# Revit family: QF_ELECTROLUXPROFESSIONAL_371110_E7MFEHDI00
name_source: partatom
category: Specialty Equipment
revit_build: Autodesk Revit 2018 (Build: 20190510_1515(x64)
units: mm (PartAtom-declared; Revit-internal decimal feet)

## family parameters
Always vertical = Yes
Cut with Voids When Loaded = No
Part Type = Normal
Room Calculation Point = No
Round Connector Dimension = Use Diameter
Shared = No
Work Plane-Based = No

## types (1)
- QF_ELECTROLUXPROFESSIONAL_371110_E7MFEHDI00
    50 Hertz Option = No
    60 Hertz Option = Yes
    Apparent Power = 10000 VA
    Conn Conduit = Yes
    Cycle = 60 Hz
    Depth = 730 mm  [stored 2.39501 ft]
    Description = 700XP Electric Multifunctional Cooker 22 Lt. - with Compound Bottom - 400V
    Direct Waste Size = 0"
    FL Amps = 14 A
    HP = 13.4 HP
    Height = 333 mm
    Indirect Waste Connection Height = 0 mm  [stored 0 ft]
    Indirect Waste Size = 0"
    Manufacturer = ELECTROLUX
    Max Overcurrent Protection = 0 A
    Min Ckt Ampacity = 0 A
    Model = 371110
    Phase = 3
    URL = www.electrolux.com/foodservice
    URL Cutsheet = www.electrolux.com/foodservice
    Volts = 400 V
    Watts = 10000 W
    Weight in Pounds = 165
    Width = 800 mm  [stored 2.62467 ft]

note: [stored X ft] marks values corroborated as IEEE doubles in the binary element streams (Revit-internal decimal feet)

## geometry (parser evidence)
native form markers: Blend x41, Sweep x2
no freeform markers — native parametric forms only
